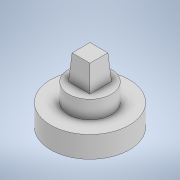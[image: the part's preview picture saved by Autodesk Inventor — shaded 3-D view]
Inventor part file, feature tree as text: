
AUTODESK INVENTOR PART (.ipt)
format: ipt  version: 2021 (Build 250183000, 183)  size: 121,856 bytes
history: native  units: mm
features: sketch x4, extrude x2, plane x1, loft x1
ambient origin geometry x8: Origin, YZ Plane, XZ Plane, XY Plane, X Axis, Y Axis, Z Axis, Center Point
bodies: Solid1 (feature_tree)
feature tree (8):
  extrude  "Extrusion1"  Depth=6.0mm TaperAngle=0.0deg
  extrude  "Extrusion2"  Depth=5.0mm TaperAngle=0.0deg
  sketch  "Sketch3"  dims[d6=6.0mm d7=6.0mm]
  plane  "Work Plane1"
  loft  "Loft1"
  sketch  "Sketch1"  dims[d0=22.0mm d1=6.0mm d2=0.0mm]
  sketch  "Sketch2"  dims[d3=12.0mm d4=5.0mm d5=0.0mm]
  sketch  "Sketch4"  dims[d8=7.0mm d9=5.0mm d10=5.0mm d11=0.0mm d12=90.0deg d13=0.0mm d14=90.0deg]
